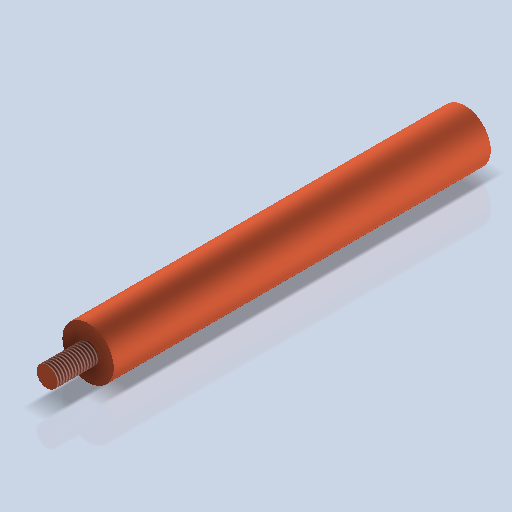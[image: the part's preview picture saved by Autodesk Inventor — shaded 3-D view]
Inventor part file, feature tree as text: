
AUTODESK INVENTOR PART (.ipt)
format: ipt  version: 2024.2 (Build 282272000, 272)  size: 256,000 bytes
history: native  units: mm
features: sketch x3, extrude x2, thread x1, hole x1
ambient origin geometry x8: Origin, YZ Plane, XZ Plane, XY Plane, X Axis, Y Axis, Z Axis, Center Point
bodies: Volumenkörper1 (feature_tree)
feature tree (7):
  extrude  "Extrusion1"  Depth=220.0mm TaperAngle=0.0deg
  extrude  "Extrusion2"  Depth=24.0mm TaperAngle=0.0deg
  thread  "Gewinde1"  [1 undecoded]
  hole  "Bohrung1"  [1 undecoded]
  sketch  "Skizze1"  dims[d0=30.0mm d1=220.0mm d2=0.0mm]
  sketch  "Skizze2"  dims[d3=12.0mm d4=24.0mm d5=0.0mm d6=24.0mm d7=0.0mm]
  sketch  "Skizze3"  dims[d8=12.0mm d9=36.0mm d10=4.0mm d11=2.0mm d12=90.0deg d13=20.0mm d14=0.0mm]
note: 2 required parameter values undecoded (feature->parameter linkage not recoverable at this tier; creation-order binding heuristic only, values carry confidence <= 0.55)
